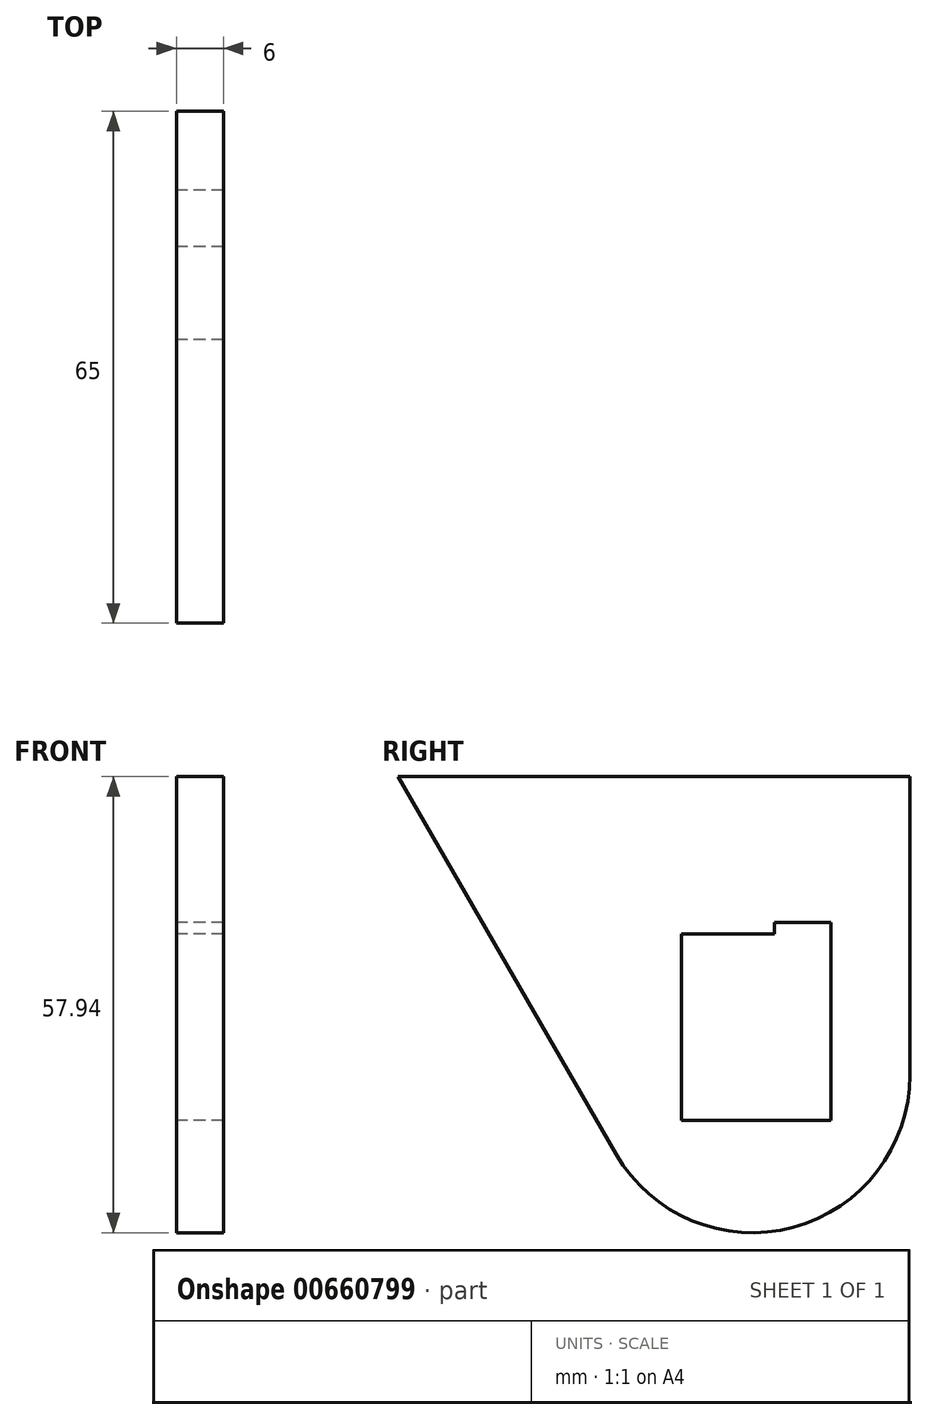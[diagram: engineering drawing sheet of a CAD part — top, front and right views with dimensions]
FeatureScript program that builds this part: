
annotation { "Feature Type Name" : "Feature", "Feature Type Description" : "" }
export const myFeature = defineFeature(function(context is Context, id is Id, definition is map)
    precondition{}
    {
        {
            var Q0;
            Q0=qCreatedBy(makeId("Right.planeOp"),FACE);
            var sketch = newSketch(context, id + "F0", { "sketchPlane" : qUnion([Q0])});
            skPoint(sketch, "E0.visualSharp", {"position": v(66.93, -159.76) * mm});
            skLineSegment(sketch, "E1", {"start": v(58.97, -89.08) * mm, "end": v(70.77, -89.08) * mm});
            skLineSegment(sketch, "E2", {"start": v(70.77, -89.08) * mm, "end": v(70.77, -87.58) * mm});
            skLineSegment(sketch, "E3", {"start": v(70.77, -87.58) * mm, "end": v(77.97, -87.58) * mm});
            skLineSegment(sketch, "E4", {"start": v(77.97, -87.58) * mm, "end": v(77.97, -112.78) * mm});
            skLineSegment(sketch, "E5", {"start": v(77.97, -112.78) * mm, "end": v(58.97, -112.78) * mm});
            skLineSegment(sketch, "E6", {"start": v(58.97, -89.08) * mm, "end": v(58.97, -112.78) * mm});
            skLineSegment(sketch, "E7", {"start": v(22.97, -69.08) * mm, "end": v(87.97, -69.08) * mm});
            skLineSegment(sketch, "E8", {"start": v(87.97, -69.08) * mm, "end": v(87.97, -107.02) * mm});
            skLineSegment(sketch, "E9", {"start": v(22.97, -69.08) * mm, "end": v(50.65, -117.02) * mm});
            skPoint(sketch, "E10.visualSharp", {"position": v(87.97, -181.67) * mm});
            skArc(sketch, "E10.filletArc", {"start": v(50.65, -117.02) * mm, "mid": v(73.14, -126.34) * mm, "end": v(87.97, -107.02) * mm});
            skSolve(sketch);
        }
        {
            var Q0;
            Q0=makeQuery(id+"F0.imprint","IMPRINT",FACE,{"disambiguationData":[TD([[makeQuery(id+"F0.imprint","IMPRINT",EDGE,{"derivedFrom":sQuery(id+"F0.wireOp",EDGE,"E1")}),1.0]])]});
            extrude(context, id + "F1", {"entities" : qUnion([Q0]), "depth" : 6 * mm, "offsetDistance" : 25.4 * mm});
        }
    });
